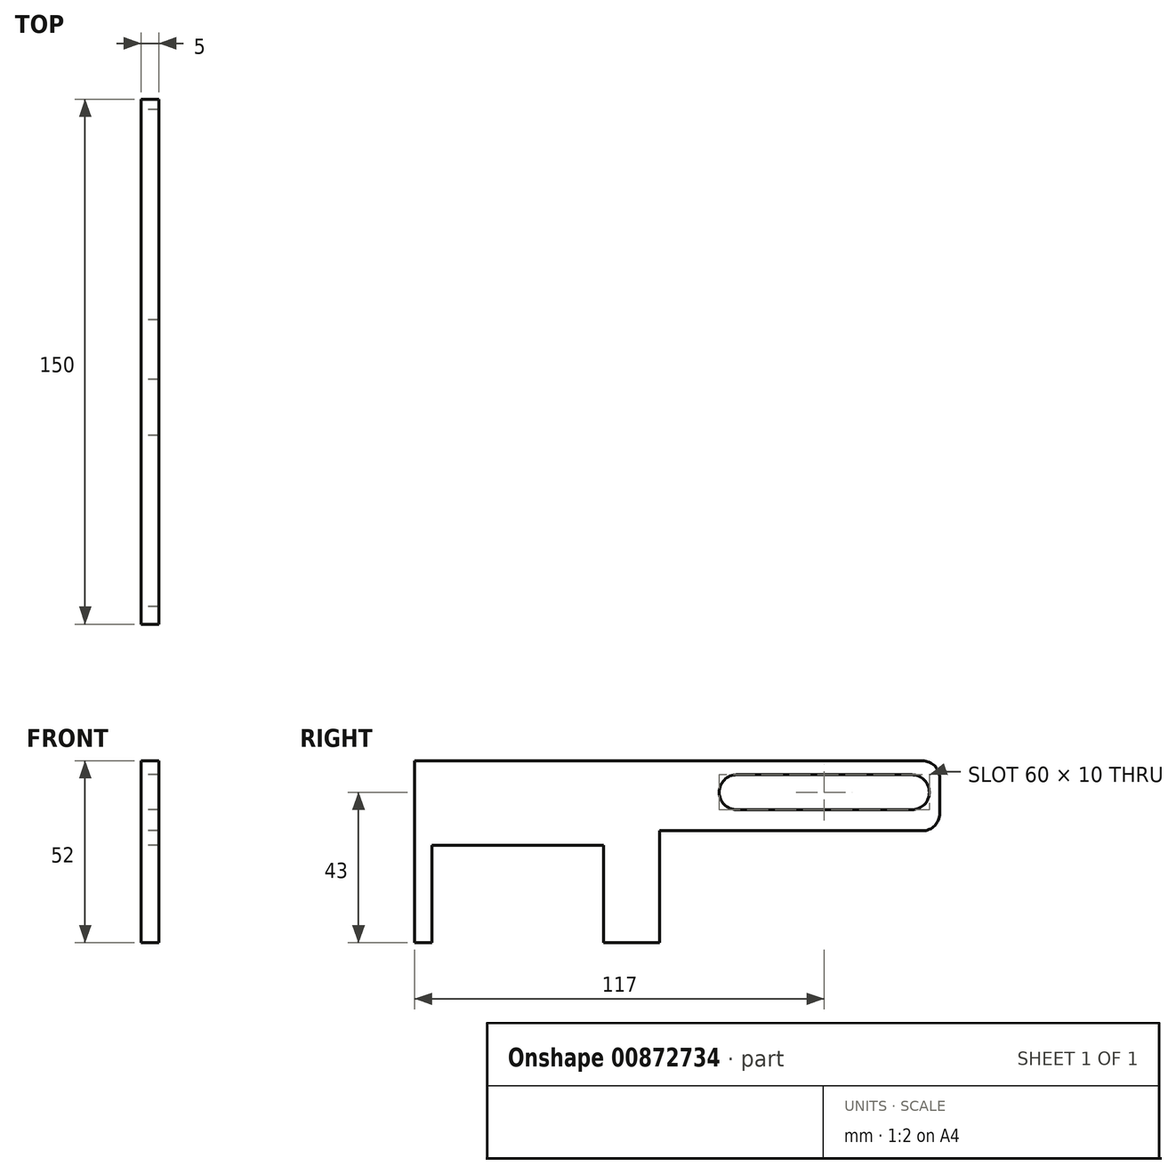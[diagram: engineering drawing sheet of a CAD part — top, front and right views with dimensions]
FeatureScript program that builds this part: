
annotation { "Feature Type Name" : "Feature", "Feature Type Description" : "" }
export const myFeature = defineFeature(function(context is Context, id is Id, definition is map)
    precondition{}
    {
        {
            var Q0;
            Q0=qCreatedBy(makeId("Right.planeOp"),FACE);
            var sketch = newSketch(context, id + "F0", { "sketchPlane" : qUnion([Q0])});
            skLineSegment(sketch, "E0.bottom", {"start": v(-35, 52) * mm, "end": v(35, 52) * mm});
            skLineSegment(sketch, "E0.top", {"start": v(-35, 0) * mm, "end": v(35, 0) * mm});
            skLineSegment(sketch, "E0.left", {"start": v(-35, 52) * mm, "end": v(-35, 0) * mm});
            skLineSegment(sketch, "E0.right", {"start": v(35, 52) * mm, "end": v(35, 0) * mm});
            skLineSegment(sketch, "E1.top", {"start": v(-24.5, 0) * mm, "end": v(19, 0) * mm});
            skLineSegment(sketch, "E2.bottom", {"start": v(35, 52) * mm, "end": v(115, 52) * mm});
            skLineSegment(sketch, "E2.top", {"start": v(35, 32) * mm, "end": v(115, 32) * mm});
            skLineSegment(sketch, "E2.left", {"start": v(35, 52) * mm, "end": v(35, 32) * mm});
            skLineSegment(sketch, "E2.right", {"start": v(115, 52) * mm, "end": v(115, 32) * mm});
            skCircle(sketch, "E3", {"center": v(107, 43) * mm, "radius": 5 * mm});
            skLineSegment(sketch, "E4.bottom", {"start": v(19, 0) * mm, "end": v(24, 0) * mm});
            skLineSegment(sketch, "E4.top", {"start": v(19, -5) * mm, "end": v(24, -5) * mm});
            skLineSegment(sketch, "E4.left", {"start": v(19, 0) * mm, "end": v(19, -5) * mm});
            skLineSegment(sketch, "E4.right", {"start": v(24, 0) * mm, "end": v(24, -5) * mm});
            skLineSegment(sketch, "E5.bottom", {"start": v(-35, 0) * mm, "end": v(-30, 0) * mm});
            skLineSegment(sketch, "E5.top", {"start": v(-35, -5) * mm, "end": v(-30, -5) * mm});
            skLineSegment(sketch, "E5.left", {"start": v(-35, 0) * mm, "end": v(-35, -5) * mm});
            skLineSegment(sketch, "E5.right", {"start": v(-30, 0) * mm, "end": v(-30, -5) * mm});
            skLineSegment(sketch, "E6.bottom", {"start": v(-30, 0) * mm, "end": v(19, 0) * mm});
            skLineSegment(sketch, "E6.top", {"start": v(-30, 27.9) * mm, "end": v(19, 27.9) * mm});
            skLineSegment(sketch, "E6.left", {"start": v(-30, 0) * mm, "end": v(-30, 27.9) * mm});
            skLineSegment(sketch, "E6.right", {"start": v(19, 0) * mm, "end": v(19, 27.9) * mm});
            skLineSegment(sketch, "E7.bottom", {"start": v(107, 48) * mm, "end": v(57, 48) * mm});
            skLineSegment(sketch, "E7.top", {"start": v(107, 38) * mm, "end": v(57, 38) * mm});
            skLineSegment(sketch, "E7.left", {"start": v(107, 48) * mm, "end": v(107, 38) * mm});
            skLineSegment(sketch, "E7.right", {"start": v(57, 48) * mm, "end": v(57, 38) * mm});
            skCircle(sketch, "E8", {"center": v(57, 43) * mm, "radius": 5 * mm});
            skSolve(sketch);
        }
        {
            var Q0;
            Q0=makeQuery(id+"F0.imprint","IMPRINT",FACE,{"disambiguationData":[TD([[makeQuery(id+"F0.imprint","IMPRINT",EDGE,{"derivedFrom":sQuery(id+"F0.wireOp",EDGE,"E2.bottom")}),-1.0]])]});
            var Q1;
            Q1=makeQuery(id+"F0.imprint","IMPRINT",FACE,{"disambiguationData":[TD([[makeQuery(id+"F0.imprint","IMPRINT",EDGE,{"derivedFrom":sQuery(id+"F0.wireOp",EDGE,"fjHMXOVk-XafM-hd5o-zvvd-RWEGUvkuaQVz.bottom")}),-1.0]])]});
            var Q2;
            Q2=makeQuery(id+"F0.imprint","IMPRINT",FACE,{"disambiguationData":[TD([[makeQuery(id+"F0.imprint","IMPRINT",EDGE,{"derivedFrom":sQuery(id+"F0.wireOp",EDGE,"s7NoRJiU-Oltl-H5VS-Ne0L-jATMiWjFW3UV.bottom")}),1.0]])]});
            var Q3;
            Q3=makeQuery(id+"F0.imprint","IMPRINT",FACE,{"disambiguationData":[TD([[makeQuery(id+"F0.imprint","IMPRINT",EDGE,{"derivedFrom":sQuery(id+"F0.wireOp",EDGE,"2CXR6XAD-CDVx-4nOY-aCdI-JKbWmf5Jsy1Z.bottom")}),-1.0]])]});
            var Q4;
            Q4=makeQuery(id+"F0.imprint","IMPRINT",FACE,{"disambiguationData":[TD([[makeQuery(id+"F0.imprint","IMPRINT",EDGE,{"derivedFrom":sQuery(id+"F0.wireOp",EDGE,"E0.bottom")}),-1.0]])]});
            var Q5;
            Q5=makeQuery(id+"F0.imprint","IMPRINT",FACE,{"disambiguationData":[TD([[makeQuery(id+"F0.imprint","IMPRINT",EDGE,{"derivedFrom":sQuery(id+"F0.wireOp",EDGE,"J0Hvdsz4-JclC-0MYD-nNIG-5zHKFkcUcQGT.bottom")}),1.0]])]});
            var Q6;
            Q6=makeQuery(id+"F0.imprint","IMPRINT",FACE,{"disambiguationData":[TD([[makeQuery(id+"F0.imprint","IMPRINT",EDGE,{"derivedFrom":sQuery(id+"F0.wireOp",EDGE,"E4.bottom")}),-1.0]])]});
            var Q7;
            Q7=makeQuery(id+"F0.imprint","IMPRINT",FACE,{"disambiguationData":[TD([[makeQuery(id+"F0.imprint","IMPRINT",EDGE,{"derivedFrom":sQuery(id+"F0.wireOp",EDGE,"RxQcjSBc-BOhR-TOVQ-KzH3-tmvJgaWQjUvC.bottom")}),1.0]])]});
            var Q8;
            Q8=makeQuery(id+"F0.imprint","IMPRINT",FACE,{"disambiguationData":[TD([[makeQuery(id+"F0.imprint","IMPRINT",EDGE,{"derivedFrom":sQuery(id+"F0.wireOp",EDGE,"E5.bottom")}),-1.0]])]});
            extrude(context, id + "F1", {"entities" : qUnion([Q0, Q1, Q2, Q3, Q4, Q5, Q6, Q7, Q8]), "depth" : 5 * mm, "offsetDistance" : 25 * mm});
        }
        {
            var Q0;
            Q0=makeQuery(id+"F1.opExtrude","SWEPT_EDGE",EDGE,{"disambiguationData":[OSD([sQuery(id+"F0.wireOp",EDGE,"E2.bottom"),sQuery(id+"F0.wireOp",EDGE,"E2.right")])]});
            var Q1;
            Q1=makeQuery(id+"F1.opExtrude","SWEPT_EDGE",EDGE,{"disambiguationData":[OSD([sQuery(id+"F0.wireOp",EDGE,"E2.top"),sQuery(id+"F0.wireOp",EDGE,"E2.right")])]});
            fillet(context, id + "F2", {"entities" : qUnion([Q0, Q1]), "radius" : 5 * mm, "tangentPropagation" : true, "allowEdgeOverflow" : false});
        }
    });
